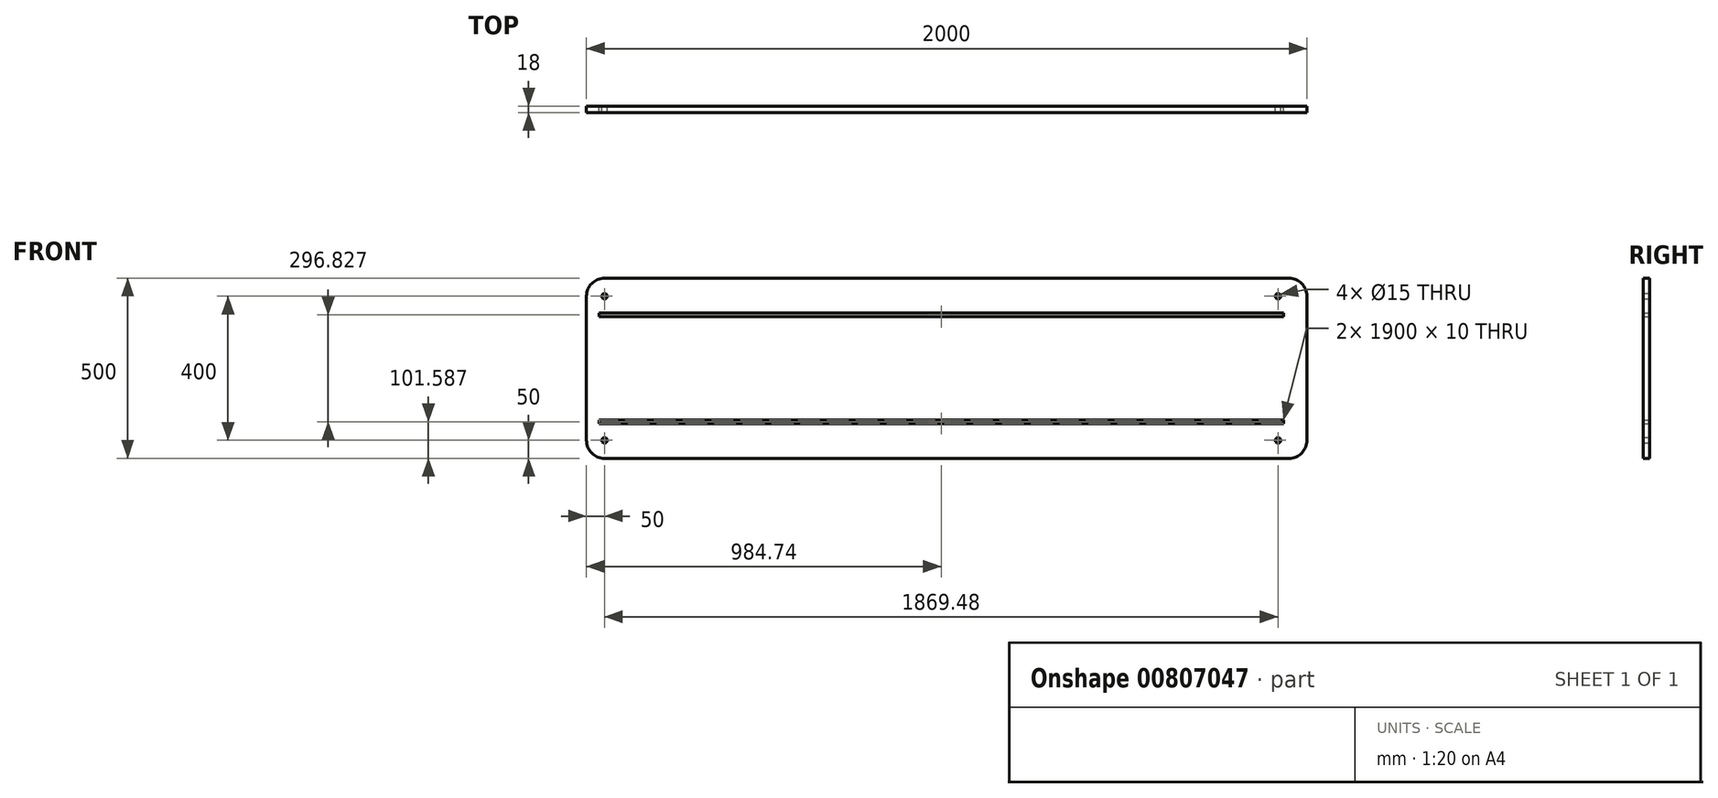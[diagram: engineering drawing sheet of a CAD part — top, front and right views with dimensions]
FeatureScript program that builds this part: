
annotation { "Feature Type Name" : "Feature", "Feature Type Description" : "" }
export const myFeature = defineFeature(function(context is Context, id is Id, definition is map)
    precondition{}
    {
        {
            var Q0;
            Q0=qCreatedBy(makeId("Front.planeOp"),FACE);
            var sketch = newSketch(context, id + "F0", { "sketchPlane" : qUnion([Q0])});
            skLineSegment(sketch, "E0.bottom", {"start": v(-934.74, 250) * mm, "end": v(965.26, 250) * mm});
            skLineSegment(sketch, "E0.top", {"start": v(-934.74, -250) * mm, "end": v(965.26, -250) * mm});
            skLineSegment(sketch, "E0.left", {"start": v(-984.74, 200) * mm, "end": v(-984.74, -200) * mm});
            skLineSegment(sketch, "E0.right", {"start": v(1015.26, 200) * mm, "end": v(1015.26, -200) * mm});
            skPoint(sketch, "E0.middle", {"position": v(15.26, 0) * mm});
            skPoint(sketch, "E1.visualSharp", {"position": v(-984.74, 250) * mm});
            skArc(sketch, "E1.filletArc", {"start": v(-934.74, 250) * mm, "mid": v(-970.1, 235.36) * mm, "end": v(-984.74, 200) * mm});
            skPoint(sketch, "E2.visualSharp", {"position": v(-984.74, -250) * mm});
            skArc(sketch, "E2.filletArc", {"start": v(-984.74, -200) * mm, "mid": v(-970.1, -235.36) * mm, "end": v(-934.74, -250) * mm});
            skPoint(sketch, "E3.visualSharp", {"position": v(1015.26, -250) * mm});
            skArc(sketch, "E3.filletArc", {"start": v(965.26, -250) * mm, "mid": v(1000.62, -235.36) * mm, "end": v(1015.26, -200) * mm});
            skPoint(sketch, "E4.visualSharp", {"position": v(1015.26, 250) * mm});
            skArc(sketch, "E4.filletArc", {"start": v(1015.26, 200) * mm, "mid": v(1000.62, 235.36) * mm, "end": v(965.26, 250) * mm});
            skLineSegment(sketch, "E5", {"start": v(15.26, 0) * mm, "end": v(1285.57, 0) * mm, "construction": true});
            skPoint(sketch, "E5.endSnap0", {"position": v(1015.26, 0) * mm});
            skLineSegment(sketch, "E6.bottom", {"start": v(-950, 153.41) * mm, "end": v(950, 153.41) * mm});
            skLineSegment(sketch, "E6.top", {"start": v(-950, 143.41) * mm, "end": v(950, 143.41) * mm});
            skLineSegment(sketch, "E6.left", {"start": v(-950, 153.41) * mm, "end": v(-950, 143.41) * mm});
            skLineSegment(sketch, "E6.right", {"start": v(950, 153.41) * mm, "end": v(950, 143.41) * mm});
            skLineSegment(sketch, "E7.MirrorCS", {"start": v(950, -153.41) * mm, "end": v(950, -143.41) * mm});
            skLineSegment(sketch, "E8.MirrorCS", {"start": v(-950, -143.41) * mm, "end": v(950, -143.41) * mm});
            skLineSegment(sketch, "E9.MirrorCS", {"start": v(-950, -153.41) * mm, "end": v(950, -153.41) * mm});
            skLineSegment(sketch, "E10.MirrorCS", {"start": v(-950, -153.41) * mm, "end": v(-950, -143.41) * mm});
            skCircle(sketch, "E11", {"center": v(-934.74, 200) * mm, "radius": 7.5 * mm});
            skLineSegment(sketch, "E12", {"start": v(0, 0) * mm, "end": v(0, 325.29) * mm, "construction": true});
            skCircle(sketch, "E13.MirrorC", {"center": v(934.74, 200) * mm, "radius": 7.5 * mm});
            skCircle(sketch, "E14.MirrorC", {"center": v(934.74, -200) * mm, "radius": 7.5 * mm});
            skCircle(sketch, "E15.MirrorC", {"center": v(-934.74, -200) * mm, "radius": 7.5 * mm});
            skSolve(sketch);
        }
        {
            var Q0;
            Q0 = qSketchRegion(id + "F0", true);
            extrude(context, id + "F1", {"entities" : qUnion([Q0]), "depth" : 18 * mm, "offsetDistance" : 25 * mm});
        }
    });
